# Revit family: XRW4811
name_source: partatom
category: Mechanical Equipment
revit_build: Autodesk Revit 2018 (Build: 20170223_1515(x64)
units: mm (PartAtom-declared; Revit-internal decimal feet)

## family parameters
Always vertical = Yes
Cut with Voids When Loaded = No
Part Type = Normal
Room Calculation Point = No
Round Connector Dimension = Use Radius
Shared = No
Work Plane-Based = No

## types (1)
- XRW 4811 PM75/24
    Cable Length (m) = As Per Specification
    Description = The compact submersible stainless steel mixer type ABS XRW 480, is specifically designed for the major mixing functions during th
homogenization of sludge and slurry.
    Fasteners = 1.4401 (AISI 316)
    Lifting Band = 1.4571 (AISI 316 Ti)
    Manufacturer = Sulzer
    Max. Subergence (mm) = 20000 mm  [stored 65.6168 ft]
    Mixer Power = 5000 W
    Model = Submersible Mixer Type ABS XRW 4811
    Motor Efficiency = 93.3%
    Motor Housing = 1.4401 (AISI 316)
    Motor Power (kW) PM75/24 = 7.5
    Motor Shaft = 1.4401 (AISI 316)
    Product Specification Link = https://www.sulzer.com
    Propeller = 1.4571 (AISI 316 Ti)
    Rated Current (A)  PM75/24 = 15.8
    Rated Voltage (V) = 400V 50Hz
    Sliding Bracket = 1.4470 or Polyamide (CF-8M)

note: [stored X ft] marks values corroborated as IEEE doubles in the binary element streams (Revit-internal decimal feet)

## geometry (parser evidence)
native form markers: Sweep x3
no freeform markers — native parametric forms only
